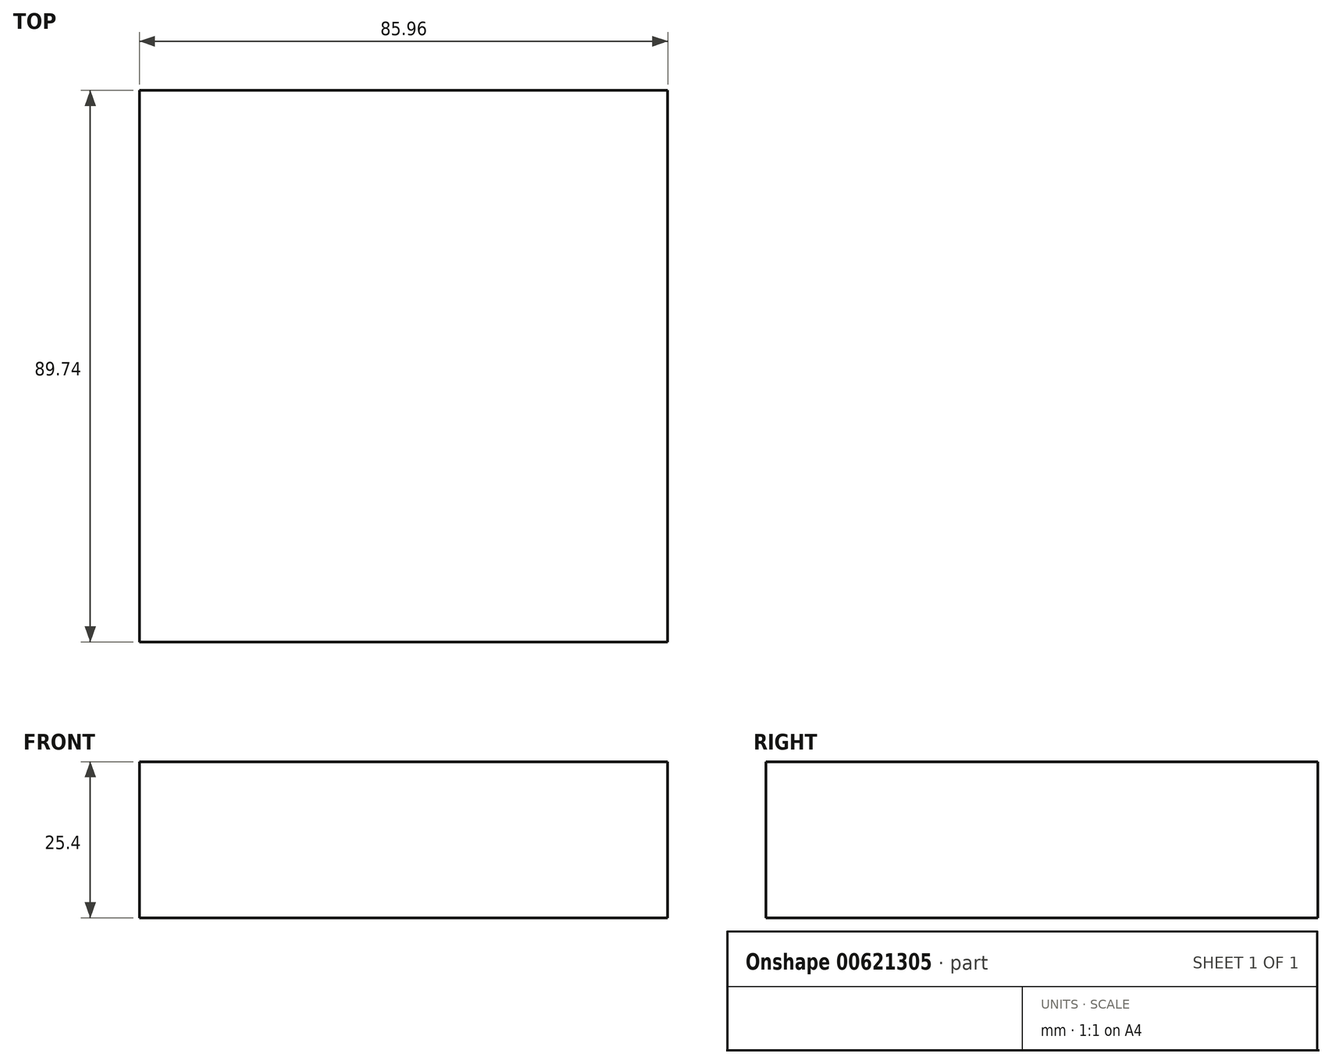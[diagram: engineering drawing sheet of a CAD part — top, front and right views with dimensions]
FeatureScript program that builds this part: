
annotation { "Feature Type Name" : "Feature", "Feature Type Description" : "" }
export const myFeature = defineFeature(function(context is Context, id is Id, definition is map)
    precondition{}
    {
        {
            var Q0;
            Q0=qCreatedBy(makeId("Top.planeOp"),FACE);
            var sketch = newSketch(context, id + "F0", { "sketchPlane" : qUnion([Q0])});
            skLineSegment(sketch, "E0.bottom", {"start": v(-139.64, 19.7) * mm, "end": v(-53.68, 19.7) * mm});
            skLineSegment(sketch, "E0.top", {"start": v(-139.64, -70.04) * mm, "end": v(-53.68, -70.04) * mm});
            skLineSegment(sketch, "E0.left", {"start": v(-139.64, 19.7) * mm, "end": v(-139.64, -70.04) * mm});
            skLineSegment(sketch, "E0.right", {"start": v(-53.68, 19.7) * mm, "end": v(-53.68, -70.04) * mm});
            skSolve(sketch);
        }
        {
            var Q0;
            Q0 = qSketchRegion(id + "F0", true);
            extrude(context, id + "F1", {"entities" : qUnion([Q0]), "depth" : 25.4 * mm, "offsetDistance" : 25.4 * mm});
        }
    });
